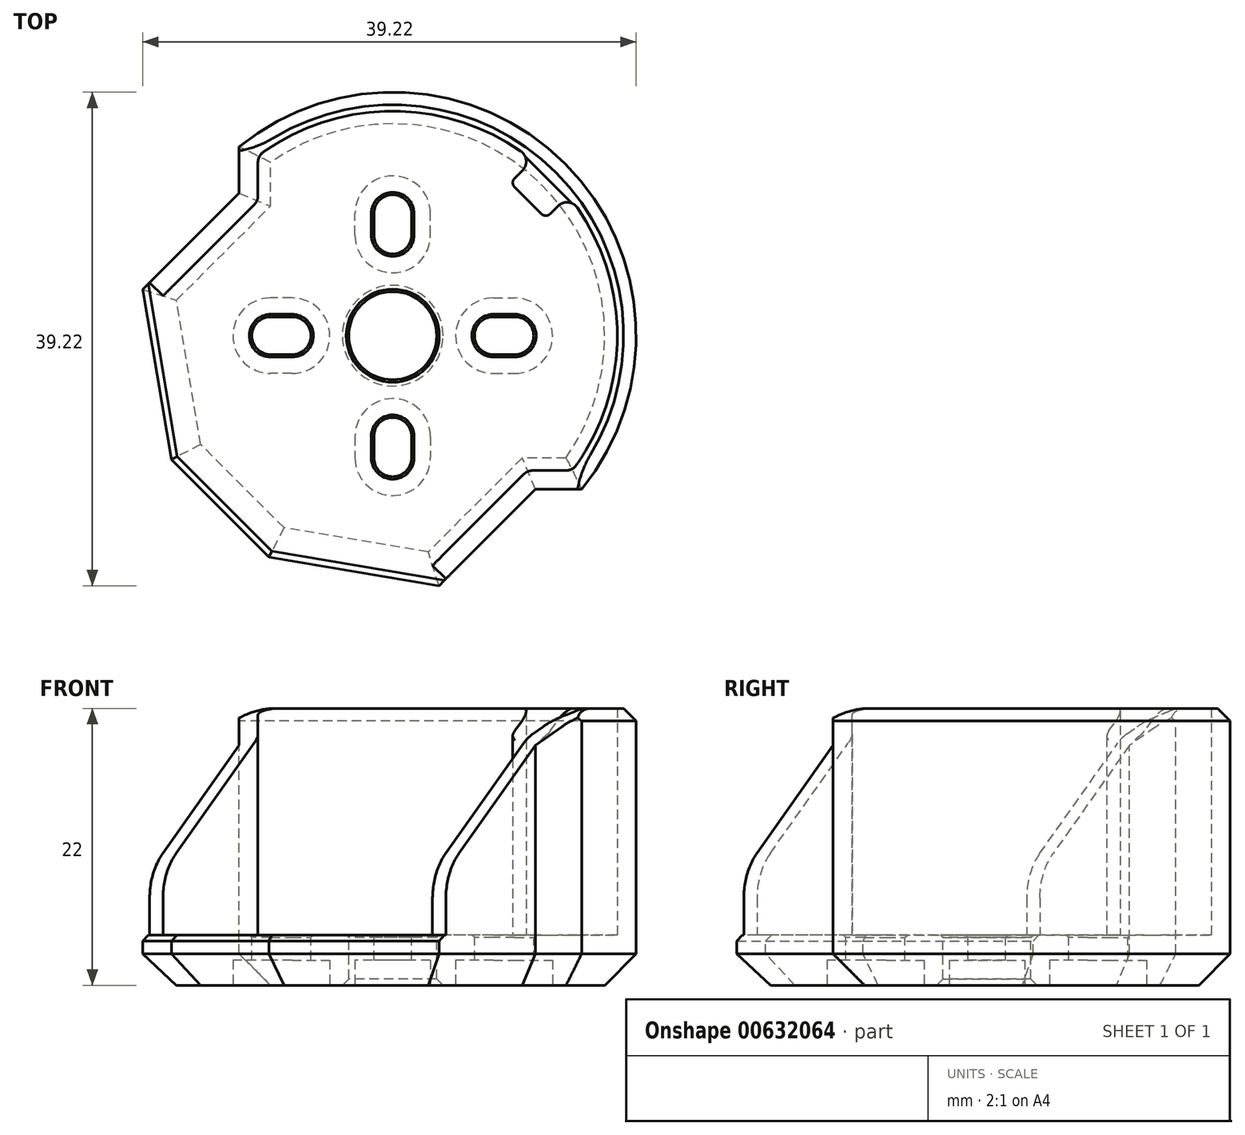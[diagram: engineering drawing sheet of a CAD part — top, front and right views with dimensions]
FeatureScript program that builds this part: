
annotation { "Feature Type Name" : "Feature", "Feature Type Description" : "" }
export const myFeature = defineFeature(function(context is Context, id is Id, definition is map)
    precondition{}
    {
        {
            var Q0;
            Q0=qCreatedBy(makeId("Top.planeOp"),FACE);
            var sketch = newSketch(context, id + "F0", { "sketchPlane" : qUnion([Q0])});
            skCircle(sketch, "E0", {"center": v(0, 0) * mm, "radius": 3.5 * mm});
            skLineSegment(sketch, "E1", {"start": v(-1.5, 8) * mm, "end": v(-1.5, 9.7) * mm});
            skArc(sketch, "E2", {"start": v(-1.5, 8) * mm, "mid": v(-1.06, 6.94) * mm, "end": v(0, 6.5) * mm});
            skArc(sketch, "E3", {"start": v(-1.5, 9.7) * mm, "mid": v(-1.06, 10.76) * mm, "end": v(0, 11.2) * mm});
            skLineSegment(sketch, "E4.MirrorCS", {"start": v(1.5, 8) * mm, "end": v(1.5, 9.7) * mm});
            skArc(sketch, "E5.MirrorCS", {"start": v(1.5, 9.7) * mm, "mid": v(1.06, 10.76) * mm, "end": v(0, 11.2) * mm});
            skArc(sketch, "E6.MirrorCS", {"start": v(1.5, 8) * mm, "mid": v(1.06, 6.94) * mm, "end": v(0, 6.5) * mm});
            skLineSegment(sketch, "E7.1.0", {"start": v(-8, 1.5) * mm, "end": v(-9.7, 1.5) * mm});
            skArc(sketch, "E7.1.1", {"start": v(-9.7, -1.5) * mm, "mid": v(-10.76, -1.06) * mm, "end": v(-11.2, 0) * mm});
            skArc(sketch, "E7.1.2", {"start": v(-8, -1.5) * mm, "mid": v(-6.94, -1.06) * mm, "end": v(-6.5, 0) * mm});
            skLineSegment(sketch, "E7.1.3", {"start": v(-8, -1.5) * mm, "end": v(-9.7, -1.5) * mm});
            skArc(sketch, "E7.1.4", {"start": v(-8, 1.5) * mm, "mid": v(-6.94, 1.06) * mm, "end": v(-6.5, 0) * mm});
            skArc(sketch, "E7.1.5", {"start": v(-9.7, 1.5) * mm, "mid": v(-10.76, 1.06) * mm, "end": v(-11.2, 0) * mm});
            skLineSegment(sketch, "E7.2.0", {"start": v(-1.5, -8) * mm, "end": v(-1.5, -9.7) * mm});
            skArc(sketch, "E7.2.1", {"start": v(1.5, -9.7) * mm, "mid": v(1.06, -10.76) * mm, "end": v(0, -11.2) * mm});
            skArc(sketch, "E7.2.2", {"start": v(1.5, -8) * mm, "mid": v(1.06, -6.94) * mm, "end": v(0, -6.5) * mm});
            skLineSegment(sketch, "E7.2.3", {"start": v(1.5, -8) * mm, "end": v(1.5, -9.7) * mm});
            skArc(sketch, "E7.2.4", {"start": v(-1.5, -8) * mm, "mid": v(-1.06, -6.94) * mm, "end": v(0, -6.5) * mm});
            skArc(sketch, "E7.2.5", {"start": v(-1.5, -9.7) * mm, "mid": v(-1.06, -10.76) * mm, "end": v(0, -11.2) * mm});
            skLineSegment(sketch, "E7.3.0", {"start": v(8, -1.5) * mm, "end": v(9.7, -1.5) * mm});
            skArc(sketch, "E7.3.1", {"start": v(9.7, 1.5) * mm, "mid": v(10.76, 1.06) * mm, "end": v(11.2, 0) * mm});
            skArc(sketch, "E7.3.2", {"start": v(8, 1.5) * mm, "mid": v(6.94, 1.06) * mm, "end": v(6.5, 0) * mm});
            skLineSegment(sketch, "E7.3.3", {"start": v(8, 1.5) * mm, "end": v(9.7, 1.5) * mm});
            skArc(sketch, "E7.3.4", {"start": v(8, -1.5) * mm, "mid": v(6.94, -1.06) * mm, "end": v(6.5, 0) * mm});
            skArc(sketch, "E7.3.5", {"start": v(9.7, -1.5) * mm, "mid": v(10.76, -1.06) * mm, "end": v(11.2, 0) * mm});
            skLineSegment(sketch, "E8", {"start": v(0, 0) * mm, "end": v(-10.71, 10.71) * mm, "construction": true});
            skLineSegment(sketch, "E9", {"start": v(-10.71, 10.71) * mm, "end": v(-18.26, 3.16) * mm});
            skArc(sketch, "E10", {"start": v(11.13, 13.96) * mm, "mid": v(0.26, 17.85) * mm, "end": v(-10.71, 14.28) * mm});
            skLineSegment(sketch, "E11", {"start": v(0, 0) * mm, "end": v(10.75, 10.75) * mm, "construction": true});
            skLineSegment(sketch, "E12", {"start": v(10.75, 10.75) * mm, "end": v(9.33, 12.16) * mm});
            skLineSegment(sketch, "E13", {"start": v(9.33, 12.16) * mm, "end": v(11.13, 13.96) * mm});
            skLineSegment(sketch, "E14.MirrorCS", {"start": v(12.16, 9.33) * mm, "end": v(13.96, 11.13) * mm});
            skLineSegment(sketch, "E15.MirrorCS", {"start": v(10.75, 10.75) * mm, "end": v(12.16, 9.33) * mm});
            skArc(sketch, "E16.MirrorCS", {"start": v(13.96, 11.13) * mm, "mid": v(17.85, 0.26) * mm, "end": v(14.28, -10.71) * mm});
            skLineSegment(sketch, "E17.MirrorCS", {"start": v(10.71, -10.71) * mm, "end": v(3.16, -18.26) * mm});
            skLineSegment(sketch, "E18", {"start": v(0, 0) * mm, "end": v(-12.66, -12.66) * mm, "construction": true});
            skLineSegment(sketch, "E19", {"start": v(-12.66, -12.66) * mm, "end": v(-16.2, -9.12) * mm});
            skLineSegment(sketch, "E20", {"start": v(-16.2, -9.12) * mm, "end": v(-18.26, 3.16) * mm});
            skLineSegment(sketch, "E21.MirrorCS", {"start": v(-9.12, -16.2) * mm, "end": v(3.16, -18.26) * mm});
            skLineSegment(sketch, "E22.MirrorCS", {"start": v(-12.66, -12.66) * mm, "end": v(-9.12, -16.2) * mm});
            skLineSegment(sketch, "E23", {"start": v(-10.71, 10.71) * mm, "end": v(-10.71, 14.28) * mm});
            skLineSegment(sketch, "E24.MirrorCS", {"start": v(10.71, -10.71) * mm, "end": v(14.28, -10.71) * mm});
            skLineSegment(sketch, "E25.5", {"start": v(-13.72, -13.72) * mm, "end": v(-17.6, -9.85) * mm});
            skArc(sketch, "E25.6", {"start": v(13.68, 13.68) * mm, "mid": v(0.99, 19.32) * mm, "end": v(-12.21, 15) * mm});
            skLineSegment(sketch, "E25.7", {"start": v(-12.21, 11.33) * mm, "end": v(-12.21, 15) * mm});
            skLineSegment(sketch, "E25.8", {"start": v(-12.21, 11.33) * mm, "end": v(-19.87, 3.68) * mm});
            skLineSegment(sketch, "E25.9", {"start": v(-17.6, -9.85) * mm, "end": v(-19.87, 3.68) * mm});
            skArc(sketch, "E26.MirrorCS", {"start": v(13.68, 13.68) * mm, "mid": v(19.32, 0.99) * mm, "end": v(15, -12.21) * mm});
            skLineSegment(sketch, "E27.MirrorCS", {"start": v(11.33, -12.21) * mm, "end": v(15, -12.21) * mm});
            skLineSegment(sketch, "E28.MirrorCS", {"start": v(11.33, -12.21) * mm, "end": v(3.68, -19.87) * mm});
            skLineSegment(sketch, "E29.MirrorCS", {"start": v(-9.85, -17.6) * mm, "end": v(3.68, -19.87) * mm});
            skLineSegment(sketch, "E30.MirrorCS", {"start": v(-13.72, -13.72) * mm, "end": v(-9.85, -17.6) * mm});
            skLineSegment(sketch, "E31", {"start": v(10.75, 10.75) * mm, "end": v(13.68, 13.68) * mm, "construction": true});
            skLineSegment(sketch, "E32", {"start": v(-12.66, -12.66) * mm, "end": v(-13.72, -13.72) * mm, "construction": true});
            skCircle(sketch, "E33", {"center": v(0, 0) * mm, "radius": 14 * mm, "construction": true});
            skLineSegment(sketch, "E34", {"start": v(-18.26, 3.16) * mm, "end": v(-19.32, 4.22) * mm});
            skLineSegment(sketch, "E35", {"start": v(3.16, -18.26) * mm, "end": v(4.22, -19.32) * mm});
            skSolve(sketch);
        }
        {
            var Q0;
            Q0=makeQuery(id+"F0.imprint","IMPRINT",FACE,{"disambiguationData":[TD([[makeQuery(id+"F0.imprint","IMPRINT",EDGE,{"derivedFrom":sQuery(id+"F0.wireOp",EDGE,"E0")}),-1.0]])]});
            var Q1;
            Q1=makeQuery(id+"F0.imprint","IMPRINT",FACE,{"disambiguationData":[TD([[makeQuery(id+"F0.imprint","IMPRINT",EDGE,{"derivedFrom":sQuery(id+"F0.wireOp",EDGE,"E9")}),-1.0]])]});
            var Q2;
            Q2=makeQuery(id+"F0.imprint","IMPRINT",FACE,{"disambiguationData":[TD([[makeQuery(id+"F0.imprint","IMPRINT",EDGE,{"derivedFrom":sQuery(id+"F0.wireOp",EDGE,"E19")}),1.0]])]});
            extrude(context, id + "F1", {"entities" : qUnion([Q0, Q1, Q2]), "oppositeDirection" : true, "depth" : 4 * mm, "offsetDistance" : 25 * mm});
        }
        {
            var Q0;
            Q0=makeQuery(id+"F0.imprint","IMPRINT",FACE,{"disambiguationData":[TD([[makeQuery(id+"F0.imprint","IMPRINT",EDGE,{"derivedFrom":sQuery(id+"F0.wireOp",EDGE,"E9")}),-1.0]])]});
            extrude(context, id + "F2", {"entities" : qUnion([Q0]), "operationType" : NewBodyOperationType.ADD, "depth" : 18 * mm, "offsetDistance" : 25 * mm});
        }
        {
            var Q0;
            Q0=makeQuery(id+"F1.opExtrude","CAP_EDGE",EDGE,{"disambiguationData":[OSD([sQuery(id+"F0.wireOp",EDGE,"E25.5"),sQuery(id+"F0.wireOp",EDGE,"E30.MirrorCS")])],"isStart":false});
            var Q1;
            Q1=makeQuery(id+"F1.opExtrude","CAP_EDGE",EDGE,{"disambiguationData":[OSD([sQuery(id+"F0.wireOp",EDGE,"E29.MirrorCS")])],"isStart":false});
            var Q2;
            Q2=makeQuery(id+"F1.opExtrude","CAP_EDGE",EDGE,{"disambiguationData":[OSD([sQuery(id+"F0.wireOp",EDGE,"E25.9")])],"isStart":false});
            var Q3;
            Q3=makeQuery(id+"F1.opExtrude","CAP_EDGE",EDGE,{"disambiguationData":[OSD([sQuery(id+"F0.wireOp",EDGE,"E25.8")])],"isStart":false});
            var Q4;
            Q4=makeQuery(id+"F1.opExtrude","CAP_EDGE",EDGE,{"disambiguationData":[OSD([sQuery(id+"F0.wireOp",EDGE,"E25.7")])],"isStart":false});
            var Q5;
            Q5=makeQuery(id+"F1.opExtrude","CAP_EDGE",EDGE,{"disambiguationData":[OSD([sQuery(id+"F0.wireOp",EDGE,"E25.6"),sQuery(id+"F0.wireOp",EDGE,"E26.MirrorCS")])],"isStart":false});
            var Q6;
            Q6=makeQuery(id+"F1.opExtrude","CAP_EDGE",EDGE,{"disambiguationData":[OSD([sQuery(id+"F0.wireOp",EDGE,"E28.MirrorCS")])],"isStart":false});
            var Q7;
            Q7=makeQuery(id+"F1.opExtrude","CAP_EDGE",EDGE,{"disambiguationData":[OSD([sQuery(id+"F0.wireOp",EDGE,"E27.MirrorCS")])],"isStart":false});
            chamfer(context, id + "F3", {"entities" : qUnion([Q0, Q1, Q2, Q3, Q4, Q5, Q6, Q7]), "width" : 2.5 * mm, "tangentPropagation" : true});
        }
        {
            var Q0;
            Q0=makeQuery(id+"F1.opExtrude","CAP_FACE",FACE,{"disambiguationData":[OSD([sQuery(id+"F0.wireOp",EDGE,"E0"),sQuery(id+"F0.wireOp",EDGE,"E1"),sQuery(id+"F0.wireOp",EDGE,"E2"),sQuery(id+"F0.wireOp",EDGE,"E3"),sQuery(id+"F0.wireOp",EDGE,"E4.MirrorCS"),sQuery(id+"F0.wireOp",EDGE,"E5.MirrorCS"),sQuery(id+"F0.wireOp",EDGE,"E6.MirrorCS"),sQuery(id+"F0.wireOp",EDGE,"E7.1.0"),sQuery(id+"F0.wireOp",EDGE,"E7.1.1"),sQuery(id+"F0.wireOp",EDGE,"E7.1.2"),sQuery(id+"F0.wireOp",EDGE,"E7.1.3"),sQuery(id+"F0.wireOp",EDGE,"E7.1.4"),sQuery(id+"F0.wireOp",EDGE,"E7.1.5"),sQuery(id+"F0.wireOp",EDGE,"E7.2.0"),sQuery(id+"F0.wireOp",EDGE,"E7.2.1"),sQuery(id+"F0.wireOp",EDGE,"E7.2.2"),sQuery(id+"F0.wireOp",EDGE,"E7.2.3"),sQuery(id+"F0.wireOp",EDGE,"E7.2.4"),sQuery(id+"F0.wireOp",EDGE,"E7.2.5"),sQuery(id+"F0.wireOp",EDGE,"E7.3.0"),sQuery(id+"F0.wireOp",EDGE,"E7.3.1"),sQuery(id+"F0.wireOp",EDGE,"E7.3.2"),sQuery(id+"F0.wireOp",EDGE,"E7.3.3"),sQuery(id+"F0.wireOp",EDGE,"E7.3.4"),sQuery(id+"F0.wireOp",EDGE,"E7.3.5"),sQuery(id+"F0.wireOp",EDGE,"E25.5"),sQuery(id+"F0.wireOp",EDGE,"E25.6"),sQuery(id+"F0.wireOp",EDGE,"E25.7"),sQuery(id+"F0.wireOp",EDGE,"E25.8"),sQuery(id+"F0.wireOp",EDGE,"E25.9"),sQuery(id+"F0.wireOp",EDGE,"E26.MirrorCS"),sQuery(id+"F0.wireOp",EDGE,"E27.MirrorCS"),sQuery(id+"F0.wireOp",EDGE,"E28.MirrorCS"),sQuery(id+"F0.wireOp",EDGE,"E29.MirrorCS"),sQuery(id+"F0.wireOp",EDGE,"E30.MirrorCS")])],"isStart":false});
            var sketch = newSketch(context, id + "F4", { "sketchPlane" : qUnion([Q0])});
            skArc(sketch, "E36.0", {"start": v(3, 9.7) * mm, "mid": v(0, 12.7) * mm, "end": v(-3, 9.7) * mm});
            skLineSegment(sketch, "E36.1", {"start": v(3, 8) * mm, "end": v(3, 9.7) * mm});
            skArc(sketch, "E36.2", {"start": v(3, 8) * mm, "mid": v(0, 5) * mm, "end": v(-3, 8) * mm});
            skLineSegment(sketch, "E36.3", {"start": v(-3, 8) * mm, "end": v(-3, 9.7) * mm});
            skLineSegment(sketch, "E37.1.0", {"start": v(-8, -3) * mm, "end": v(-9.7, -3) * mm});
            skArc(sketch, "E37.1.1", {"start": v(-8, 3) * mm, "mid": v(-5, 0) * mm, "end": v(-8, -3) * mm});
            skLineSegment(sketch, "E37.1.2", {"start": v(-8, 3) * mm, "end": v(-9.7, 3) * mm});
            skArc(sketch, "E37.1.3", {"start": v(-9.7, 3) * mm, "mid": v(-12.7, 0) * mm, "end": v(-9.7, -3) * mm});
            skLineSegment(sketch, "E37.2.0", {"start": v(3, -8) * mm, "end": v(3, -9.7) * mm});
            skArc(sketch, "E37.2.1", {"start": v(-3, -8) * mm, "mid": v(0, -5) * mm, "end": v(3, -8) * mm});
            skLineSegment(sketch, "E37.2.2", {"start": v(-3, -8) * mm, "end": v(-3, -9.7) * mm});
            skArc(sketch, "E37.2.3", {"start": v(-3, -9.7) * mm, "mid": v(0, -12.7) * mm, "end": v(3, -9.7) * mm});
            skLineSegment(sketch, "E37.3.0", {"start": v(8, 3) * mm, "end": v(9.7, 3) * mm});
            skArc(sketch, "E37.3.1", {"start": v(8, -3) * mm, "mid": v(5, 0) * mm, "end": v(8, 3) * mm});
            skLineSegment(sketch, "E37.3.2", {"start": v(8, -3) * mm, "end": v(9.7, -3) * mm});
            skArc(sketch, "E37.3.3", {"start": v(9.7, -3) * mm, "mid": v(12.7, 0) * mm, "end": v(9.7, 3) * mm});
            skPoint(sketch, "E37.center", {"position": v(0, 0) * mm});
            skLineSegment(sketch, "E38", {"start": v(3, 8) * mm, "end": v(8, 3) * mm});
            skLineSegment(sketch, "E39", {"start": v(8, -3) * mm, "end": v(3, -8) * mm});
            skLineSegment(sketch, "E40", {"start": v(-3, -8) * mm, "end": v(-8, -3) * mm});
            skLineSegment(sketch, "E41", {"start": v(-8, 3) * mm, "end": v(-3, 8) * mm});
            skSolve(sketch);
        }
        {
            var Q0;
            Q0=makeQuery(id+"F4.imprint","IMPRINT",FACE,{"disambiguationData":[TD([[makeQuery(id+"F4.imprint","IMPRINT",EDGE,{"derivedFrom":sQuery(id+"F4.wireOp",EDGE,"E36.0")}),1.0]])]});
            var Q1;
            Q1=makeQuery(id+"F4.imprint","IMPRINT",FACE,{"disambiguationData":[TD([[makeQuery(id+"F4.imprint","IMPRINT",EDGE,{"derivedFrom":sQuery(id+"F4.wireOp",EDGE,"E37.1.0")}),-1.0]])]});
            var Q2;
            Q2=makeQuery(id+"F4.imprint","IMPRINT",FACE,{"disambiguationData":[TD([[makeQuery(id+"F4.imprint","IMPRINT",EDGE,{"derivedFrom":sQuery(id+"F4.wireOp",EDGE,"E37.2.0")}),-1.0]])]});
            var Q3;
            Q3=makeQuery(id+"F4.imprint","IMPRINT",FACE,{"disambiguationData":[TD([[makeQuery(id+"F4.imprint","IMPRINT",EDGE,{"derivedFrom":sQuery(id+"F4.wireOp",EDGE,"E37.3.0")}),-1.0]])]});
            extrude(context, id + "F5", {"entities" : qUnion([Q0, Q1, Q2, Q3]), "operationType" : NewBodyOperationType.REMOVE, "oppositeDirection" : true, "depth" : 2 * mm, "offsetDistance" : 25 * mm});
        }
        {
            var Q0;
            Q0=makeQuery(id+"F5.boolean.opBoolean","COPY",EDGE,{"derivedFrom":makeQuery(id+"F5.opExtrude","CAP_EDGE",EDGE,{"disambiguationData":[OSD([sQuery(id+"F4.wireOp",EDGE,"E41")])],"isStart":true})});
            var Q1;
            Q1=makeQuery(id+"F5.boolean.opBoolean","COPY",EDGE,{"derivedFrom":makeQuery(id+"F5.opExtrude","CAP_EDGE",EDGE,{"disambiguationData":[OSD([sQuery(id+"F4.wireOp",EDGE,"E36.3")])],"isStart":true})});
            var Q2;
            Q2=makeQuery(id+"F5.boolean.opBoolean","COPY",EDGE,{"derivedFrom":makeQuery(id+"F5.opExtrude","CAP_EDGE",EDGE,{"disambiguationData":[OSD([sQuery(id+"F4.wireOp",EDGE,"E36.0")])],"isStart":true})});
            var Q3;
            Q3=makeQuery(id+"F5.boolean.opBoolean","COPY",EDGE,{"derivedFrom":makeQuery(id+"F5.opExtrude","CAP_EDGE",EDGE,{"disambiguationData":[OSD([sQuery(id+"F4.wireOp",EDGE,"E38")])],"isStart":true})});
            var Q4;
            Q4=makeQuery(id+"F5.boolean.opBoolean","COPY",EDGE,{"derivedFrom":makeQuery(id+"F5.opExtrude","CAP_EDGE",EDGE,{"disambiguationData":[OSD([sQuery(id+"F4.wireOp",EDGE,"E36.1")])],"isStart":true})});
            var Q5;
            Q5=makeQuery(id+"F5.boolean.opBoolean","COPY",EDGE,{"derivedFrom":makeQuery(id+"F5.opExtrude","CAP_EDGE",EDGE,{"disambiguationData":[OSD([sQuery(id+"F4.wireOp",EDGE,"E37.3.0")])],"isStart":true})});
            var Q6;
            Q6=makeQuery(id+"F5.boolean.opBoolean","COPY",EDGE,{"derivedFrom":makeQuery(id+"F5.opExtrude","CAP_EDGE",EDGE,{"disambiguationData":[OSD([sQuery(id+"F4.wireOp",EDGE,"E37.3.3")])],"isStart":true})});
            var Q7;
            Q7=makeQuery(id+"F5.boolean.opBoolean","COPY",EDGE,{"derivedFrom":makeQuery(id+"F5.opExtrude","CAP_EDGE",EDGE,{"disambiguationData":[OSD([sQuery(id+"F4.wireOp",EDGE,"E37.3.2")])],"isStart":true})});
            var Q8;
            Q8=makeQuery(id+"F5.boolean.opBoolean","COPY",EDGE,{"derivedFrom":makeQuery(id+"F5.opExtrude","CAP_EDGE",EDGE,{"disambiguationData":[OSD([sQuery(id+"F4.wireOp",EDGE,"E39")])],"isStart":true})});
            var Q9;
            Q9=makeQuery(id+"F5.boolean.opBoolean","COPY",EDGE,{"derivedFrom":makeQuery(id+"F5.opExtrude","CAP_EDGE",EDGE,{"disambiguationData":[OSD([sQuery(id+"F4.wireOp",EDGE,"E37.2.0")])],"isStart":true})});
            var Q10;
            Q10=makeQuery(id+"F5.boolean.opBoolean","COPY",EDGE,{"derivedFrom":makeQuery(id+"F5.opExtrude","CAP_EDGE",EDGE,{"disambiguationData":[OSD([sQuery(id+"F4.wireOp",EDGE,"E37.2.3")])],"isStart":true})});
            var Q11;
            Q11=makeQuery(id+"F5.boolean.opBoolean","COPY",EDGE,{"derivedFrom":makeQuery(id+"F5.opExtrude","CAP_EDGE",EDGE,{"disambiguationData":[OSD([sQuery(id+"F4.wireOp",EDGE,"E37.2.2")])],"isStart":true})});
            var Q12;
            Q12=makeQuery(id+"F5.boolean.opBoolean","COPY",EDGE,{"derivedFrom":makeQuery(id+"F5.opExtrude","CAP_EDGE",EDGE,{"disambiguationData":[OSD([sQuery(id+"F4.wireOp",EDGE,"E40")])],"isStart":true})});
            var Q13;
            Q13=makeQuery(id+"F5.boolean.opBoolean","COPY",EDGE,{"derivedFrom":makeQuery(id+"F5.opExtrude","CAP_EDGE",EDGE,{"disambiguationData":[OSD([sQuery(id+"F4.wireOp",EDGE,"E37.1.0")])],"isStart":true})});
            var Q14;
            Q14=makeQuery(id+"F5.boolean.opBoolean","COPY",EDGE,{"derivedFrom":makeQuery(id+"F5.opExtrude","CAP_EDGE",EDGE,{"disambiguationData":[OSD([sQuery(id+"F4.wireOp",EDGE,"E37.1.2")])],"isStart":true})});
            var Q15;
            Q15=makeQuery(id+"F5.boolean.opBoolean","COPY",EDGE,{"derivedFrom":makeQuery(id+"F5.opExtrude","CAP_EDGE",EDGE,{"disambiguationData":[OSD([sQuery(id+"F4.wireOp",EDGE,"E37.1.3")])],"isStart":true})});
            var Q16;
            Q16=makeQuery(id+"F1.opExtrude","CAP_EDGE",EDGE,{"disambiguationData":[OSD([sQuery(id+"F0.wireOp",EDGE,"E0")])],"isStart":false});
            chamfer(context, id + "F6", {"entities" : qUnion([Q0, Q1, Q2, Q3, Q4, Q5, Q6, Q7, Q8, Q9, Q10, Q11, Q12, Q13, Q14, Q15, Q16]), "width" : 0.5 * mm, "tangentPropagation" : true});
        }
        {
            var Q0;
            Q0=makeQuery(id+"F2.opExtrude","CAP_EDGE",EDGE,{"disambiguationData":[OSD([sQuery(id+"F0.wireOp",EDGE,"E25.6"),sQuery(id+"F0.wireOp",EDGE,"E26.MirrorCS")])],"isStart":false});
            chamfer(context, id + "F7", {"entities" : qUnion([Q0]), "width" : 1 * mm, "tangentPropagation" : true});
        }
        {
            var Q0;
            Q0=makeQuery(id+"F1.opExtrude","CAP_EDGE",EDGE,{"disambiguationData":[OSD([sQuery(id+"F0.wireOp",EDGE,"E25.5"),sQuery(id+"F0.wireOp",EDGE,"E30.MirrorCS")])],"isStart":true});
            var Q1;
            Q1=makeQuery(id+"F1.opExtrude","CAP_EDGE",EDGE,{"disambiguationData":[OSD([sQuery(id+"F0.wireOp",EDGE,"E29.MirrorCS")])],"isStart":true});
            var Q2;
            Q2=makeQuery(id+"F1.opExtrude","CAP_EDGE",EDGE,{"disambiguationData":[OSD([sQuery(id+"F0.wireOp",EDGE,"E25.9")])],"isStart":true});
            chamfer(context, id + "F8", {"entities" : qUnion([Q0, Q1, Q2]), "width" : 0.5 * mm, "tangentPropagation" : true});
        }
        {
            var Q0;
            Q0=makeQuery(id+"F2.opExtrude","SWEPT_EDGE",EDGE,{"disambiguationData":[OSD([sQuery(id+"F0.wireOp",EDGE,"E10"),sQuery(id+"F0.wireOp",EDGE,"E23")])]});
            var Q1;
            Q1=makeQuery(id+"F2.opExtrude","SWEPT_EDGE",EDGE,{"disambiguationData":[OSD([sQuery(id+"F0.wireOp",EDGE,"E9"),sQuery(id+"F0.wireOp",EDGE,"E23")])]});
            var Q2;
            Q2=makeQuery(id+"F2.opExtrude","SWEPT_EDGE",EDGE,{"disambiguationData":[OSD([sQuery(id+"F0.wireOp",EDGE,"E10"),sQuery(id+"F0.wireOp",EDGE,"E13")])]});
            var Q3;
            Q3=makeQuery(id+"F2.opExtrude","SWEPT_EDGE",EDGE,{"disambiguationData":[OSD([sQuery(id+"F0.wireOp",EDGE,"E14.MirrorCS"),sQuery(id+"F0.wireOp",EDGE,"E16.MirrorCS")])]});
            var Q4;
            Q4=makeQuery(id+"F2.opExtrude","SWEPT_EDGE",EDGE,{"disambiguationData":[OSD([sQuery(id+"F0.wireOp",EDGE,"E16.MirrorCS"),sQuery(id+"F0.wireOp",EDGE,"E24.MirrorCS")])]});
            var Q5;
            Q5=makeQuery(id+"F2.opExtrude","SWEPT_EDGE",EDGE,{"disambiguationData":[OSD([sQuery(id+"F0.wireOp",EDGE,"E17.MirrorCS"),sQuery(id+"F0.wireOp",EDGE,"E24.MirrorCS")])]});
            fillet(context, id + "F9", {"entities" : qUnion([Q0, Q1, Q2, Q3, Q4, Q5]), "radius" : 1 * mm, "tangentPropagation" : true, "allowEdgeOverflow" : false});
        }
        {
            var Q0;
            Q0=makeQuery(id+"F2.opExtrude","CAP_EDGE",EDGE,{"disambiguationData":[OSD([sQuery(id+"F0.wireOp",EDGE,"E12"),sQuery(id+"F0.wireOp",EDGE,"E15.MirrorCS")])],"isStart":false});
            chamfer(context, id + "F10", {"entities" : qUnion([Q0]), "width" : 2.3 * mm, "tangentPropagation" : true});
        }
        {
            var Q0;
            Q0=makeQuery(id+"F2.opExtrude","CAP_EDGE",EDGE,{"disambiguationData":[OSD([sQuery(id+"F0.wireOp",EDGE,"E34")])],"isStart":false});
            var Q1;
            Q1=makeQuery(id+"F2.opExtrude","CAP_EDGE",EDGE,{"disambiguationData":[OSD([sQuery(id+"F0.wireOp",EDGE,"E35")])],"isStart":false});
            chamfer(context, id + "F11", {"entities" : qUnion([Q0, Q1]), "width" : 13 * mm, "tangentPropagation" : true});
        }
        {
            var Q0;
            {var subQ0=sQuery(id+"F0.wireOp",EDGE,"E35");Q0=makeQuery(id+"F11.opChamfer","BLEND_EDGE",EDGE,{"blendedFrom":[makeQuery(id+"F2.opExtrude","CAP_EDGE",EDGE,{"disambiguationData":[OSD([subQ0])],"isStart":false}),makeQuery(id+"F2.opExtrude","SWEPT_FACE",FACE,{"disambiguationData":[OSD([subQ0])]})],"blendedInto":[makeQuery(id+"F2.opExtrude","SWEPT_FACE",FACE,{"disambiguationData":[OSD([subQ0])]})]});}
            var Q1;
            {var subQ0=sQuery(id+"F0.wireOp",EDGE,"E34");Q1=makeQuery(id+"F11.opChamfer","BLEND_EDGE",EDGE,{"blendedFrom":[makeQuery(id+"F2.opExtrude","CAP_EDGE",EDGE,{"disambiguationData":[OSD([subQ0])],"isStart":false}),makeQuery(id+"F2.opExtrude","SWEPT_FACE",FACE,{"disambiguationData":[OSD([subQ0])]})],"blendedInto":[makeQuery(id+"F2.opExtrude","SWEPT_FACE",FACE,{"disambiguationData":[OSD([subQ0])]})]});}
            var Q2;
            {var subQ0=sQuery(id+"F0.wireOp",EDGE,"E35");Q2=makeQuery(id+"F11.opChamfer","BLEND_EDGE",EDGE,{"blendedFrom":[makeQuery(id+"F2.opExtrude","CAP_EDGE",EDGE,{"disambiguationData":[OSD([subQ0])],"isStart":false}),makeQuery(id+"F2.opExtrude","CAP_FACE",FACE,{"disambiguationData":[OSD([sQuery(id+"F0.wireOp",EDGE,"E9"),sQuery(id+"F0.wireOp",EDGE,"E10"),sQuery(id+"F0.wireOp",EDGE,"E12"),sQuery(id+"F0.wireOp",EDGE,"E13"),sQuery(id+"F0.wireOp",EDGE,"E14.MirrorCS"),sQuery(id+"F0.wireOp",EDGE,"E15.MirrorCS"),sQuery(id+"F0.wireOp",EDGE,"E16.MirrorCS"),sQuery(id+"F0.wireOp",EDGE,"E17.MirrorCS"),sQuery(id+"F0.wireOp",EDGE,"E23"),sQuery(id+"F0.wireOp",EDGE,"E24.MirrorCS"),sQuery(id+"F0.wireOp",EDGE,"E25.6"),sQuery(id+"F0.wireOp",EDGE,"E25.7"),sQuery(id+"F0.wireOp",EDGE,"E25.8"),sQuery(id+"F0.wireOp",EDGE,"E26.MirrorCS"),sQuery(id+"F0.wireOp",EDGE,"E27.MirrorCS"),sQuery(id+"F0.wireOp",EDGE,"E28.MirrorCS"),sQuery(id+"F0.wireOp",EDGE,"E34"),subQ0])],"isStart":false})],"blendedInto":[makeQuery(id+"F2.opExtrude","CAP_FACE",FACE,{"disambiguationData":[OSD([sQuery(id+"F0.wireOp",EDGE,"E9"),sQuery(id+"F0.wireOp",EDGE,"E10"),sQuery(id+"F0.wireOp",EDGE,"E12"),sQuery(id+"F0.wireOp",EDGE,"E13"),sQuery(id+"F0.wireOp",EDGE,"E14.MirrorCS"),sQuery(id+"F0.wireOp",EDGE,"E15.MirrorCS"),sQuery(id+"F0.wireOp",EDGE,"E16.MirrorCS"),sQuery(id+"F0.wireOp",EDGE,"E17.MirrorCS"),sQuery(id+"F0.wireOp",EDGE,"E23"),sQuery(id+"F0.wireOp",EDGE,"E24.MirrorCS"),sQuery(id+"F0.wireOp",EDGE,"E25.6"),sQuery(id+"F0.wireOp",EDGE,"E25.7"),sQuery(id+"F0.wireOp",EDGE,"E25.8"),sQuery(id+"F0.wireOp",EDGE,"E26.MirrorCS"),sQuery(id+"F0.wireOp",EDGE,"E27.MirrorCS"),sQuery(id+"F0.wireOp",EDGE,"E28.MirrorCS"),sQuery(id+"F0.wireOp",EDGE,"E34"),subQ0])],"isStart":false})]});}
            var Q3;
            {var subQ0=sQuery(id+"F0.wireOp",EDGE,"E34");Q3=makeQuery(id+"F11.opChamfer","BLEND_EDGE",EDGE,{"blendedFrom":[makeQuery(id+"F2.opExtrude","CAP_EDGE",EDGE,{"disambiguationData":[OSD([subQ0])],"isStart":false}),makeQuery(id+"F2.opExtrude","CAP_FACE",FACE,{"disambiguationData":[OSD([sQuery(id+"F0.wireOp",EDGE,"E9"),sQuery(id+"F0.wireOp",EDGE,"E10"),sQuery(id+"F0.wireOp",EDGE,"E12"),sQuery(id+"F0.wireOp",EDGE,"E13"),sQuery(id+"F0.wireOp",EDGE,"E14.MirrorCS"),sQuery(id+"F0.wireOp",EDGE,"E15.MirrorCS"),sQuery(id+"F0.wireOp",EDGE,"E16.MirrorCS"),sQuery(id+"F0.wireOp",EDGE,"E17.MirrorCS"),sQuery(id+"F0.wireOp",EDGE,"E23"),sQuery(id+"F0.wireOp",EDGE,"E24.MirrorCS"),sQuery(id+"F0.wireOp",EDGE,"E25.6"),sQuery(id+"F0.wireOp",EDGE,"E25.7"),sQuery(id+"F0.wireOp",EDGE,"E25.8"),sQuery(id+"F0.wireOp",EDGE,"E26.MirrorCS"),sQuery(id+"F0.wireOp",EDGE,"E27.MirrorCS"),sQuery(id+"F0.wireOp",EDGE,"E28.MirrorCS"),subQ0,sQuery(id+"F0.wireOp",EDGE,"E35")])],"isStart":false})],"blendedInto":[makeQuery(id+"F2.opExtrude","CAP_FACE",FACE,{"disambiguationData":[OSD([sQuery(id+"F0.wireOp",EDGE,"E9"),sQuery(id+"F0.wireOp",EDGE,"E10"),sQuery(id+"F0.wireOp",EDGE,"E12"),sQuery(id+"F0.wireOp",EDGE,"E13"),sQuery(id+"F0.wireOp",EDGE,"E14.MirrorCS"),sQuery(id+"F0.wireOp",EDGE,"E15.MirrorCS"),sQuery(id+"F0.wireOp",EDGE,"E16.MirrorCS"),sQuery(id+"F0.wireOp",EDGE,"E17.MirrorCS"),sQuery(id+"F0.wireOp",EDGE,"E23"),sQuery(id+"F0.wireOp",EDGE,"E24.MirrorCS"),sQuery(id+"F0.wireOp",EDGE,"E25.6"),sQuery(id+"F0.wireOp",EDGE,"E25.7"),sQuery(id+"F0.wireOp",EDGE,"E25.8"),sQuery(id+"F0.wireOp",EDGE,"E26.MirrorCS"),sQuery(id+"F0.wireOp",EDGE,"E27.MirrorCS"),sQuery(id+"F0.wireOp",EDGE,"E28.MirrorCS"),subQ0,sQuery(id+"F0.wireOp",EDGE,"E35")])],"isStart":false})]});}
            fillet(context, id + "F12", {"entities" : qUnion([Q0, Q1, Q2, Q3]), "radius" : 5 * mm, "tangentPropagation" : true, "allowEdgeOverflow" : false});
        }
        {
            var Q0;
            Q0=makeQuery(id+"F2.opExtrude","SWEPT_EDGE",EDGE,{"disambiguationData":[OSD([sQuery(id+"F0.wireOp",EDGE,"E14.MirrorCS"),sQuery(id+"F0.wireOp",EDGE,"E15.MirrorCS")])]});
            var Q1;
            Q1=makeQuery(id+"F2.opExtrude","SWEPT_EDGE",EDGE,{"disambiguationData":[OSD([sQuery(id+"F0.wireOp",EDGE,"E12"),sQuery(id+"F0.wireOp",EDGE,"E13")])]});
            var Q2;
            {var subQ0=sQuery(id+"F0.wireOp",EDGE,"E15.MirrorCS");var subQ1=sQuery(id+"F0.wireOp",EDGE,"E12");Q2=makeQuery(id+"F10.opChamfer","BLEND_EDGE",EDGE,{"blendedFrom":[makeQuery(id+"F2.opExtrude","CAP_EDGE",EDGE,{"disambiguationData":[OSD([subQ1,subQ0])],"isStart":false}),makeQuery(id+"F2.opExtrude","SWEPT_FACE",FACE,{"disambiguationData":[OSD([subQ1,subQ0])]})],"blendedInto":[makeQuery(id+"F2.opExtrude","SWEPT_FACE",FACE,{"disambiguationData":[OSD([subQ1,subQ0])]})]});}
            fillet(context, id + "F13", {"entities" : qUnion([Q0, Q1, Q2]), "radius" : 0.5 * mm, "tangentPropagation" : true, "allowEdgeOverflow" : false});
        }
        {
            var Q0;
            Q0=makeQuery(id+"F1.opExtrude","CAP_EDGE",EDGE,{"disambiguationData":[OSD([sQuery(id+"F0.wireOp",EDGE,"E7.1.2"),sQuery(id+"F0.wireOp",EDGE,"E7.1.4")])],"isStart":true});
            var Q1;
            Q1=makeQuery(id+"F1.opExtrude","CAP_EDGE",EDGE,{"disambiguationData":[OSD([sQuery(id+"F0.wireOp",EDGE,"E0")])],"isStart":true});
            var Q2;
            Q2=makeQuery(id+"F1.opExtrude","CAP_EDGE",EDGE,{"disambiguationData":[OSD([sQuery(id+"F0.wireOp",EDGE,"E2"),sQuery(id+"F0.wireOp",EDGE,"E6.MirrorCS")])],"isStart":true});
            var Q3;
            Q3=makeQuery(id+"F1.opExtrude","CAP_EDGE",EDGE,{"disambiguationData":[OSD([sQuery(id+"F0.wireOp",EDGE,"E7.2.2"),sQuery(id+"F0.wireOp",EDGE,"E7.2.4")])],"isStart":true});
            var Q4;
            Q4=makeQuery(id+"F1.opExtrude","CAP_EDGE",EDGE,{"disambiguationData":[OSD([sQuery(id+"F0.wireOp",EDGE,"E7.3.2"),sQuery(id+"F0.wireOp",EDGE,"E7.3.4")])],"isStart":true});
            chamfer(context, id + "F14", {"entities" : qUnion([Q0, Q1, Q2, Q3, Q4]), "width" : 0.2 * mm, "tangentPropagation" : true});
        }
    });
